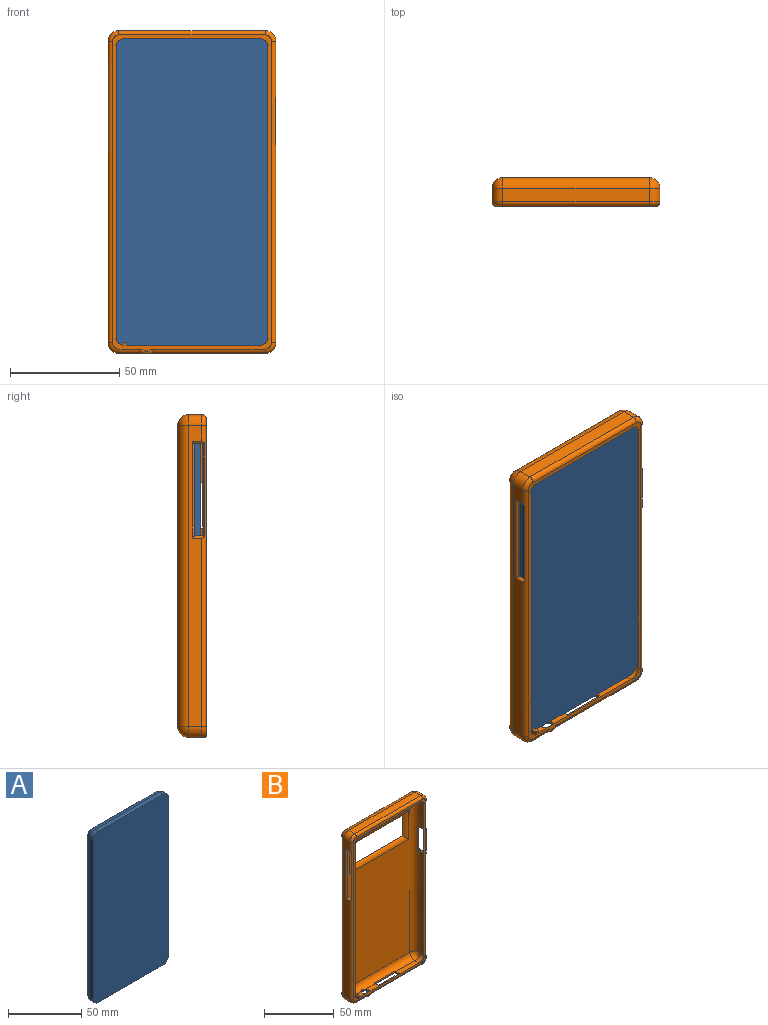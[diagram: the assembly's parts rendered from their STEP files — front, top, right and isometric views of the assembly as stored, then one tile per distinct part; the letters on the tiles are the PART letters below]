
ASSEMBLY  parts=2 mates=1
PART A: 18 faces, bbox 72.1x8.3x142.4 mm
  f0: plane 132.24x3.22mm, normal (1,0,0), area 425.8mm2, adj f4,f6,f9,f10
  f1: plane 61.94x3.22mm, normal (0,0,1), area 199.4mm2, adj f4,f6,f7,f13
  f2: plane 132.24x3.22mm, normal (-1,0,0), area 425.8mm2, adj f4,f7,f8,f17
  f3: plane 61.94x3.22mm, normal (0,0,-1), area 199.4mm2, adj f4,f8,f9,f14
  f4: plane 142.4x72.1mm, normal (0,-1,0), area 10244.9mm2, adj f0,f1,f2,f3,f6,f7,f8,f9
  f5: plane 132.24x61.94mm, normal (0,1,0), area 8190.9mm2, adj f10,f13,f14,f17
  f6: cylinder r=5.08mm len=5.08mm, axis (0,-1,0), area 25.7mm2, adj f0,f1,f4,f11
  f7: cylinder r=5.08mm len=5.08mm, axis (0,1,0), area 25.7mm2, adj f1,f2,f4,f15
  f8: cylinder r=5.08mm len=5.08mm, axis (0,-1,0), area 25.7mm2, adj f2,f3,f4,f16
  f9: cylinder r=5.08mm len=5.08mm, axis (0,1,0), area 25.7mm2, adj f0,f3,f4,f12
  f10: cylinder r=5.08mm len=132.24mm, axis (0,0,1), area 1055.2mm2, adj f0,f5,f11,f12
  f11: sphere r=5.08mm, area 40.5mm2, adj f6,f10,f13
  f12: sphere r=5.08mm, area 40.5mm2, adj f9,f10,f14
  f13: cylinder r=5.08mm len=61.94mm, axis (-1,0,0), area 494.3mm2, adj f1,f5,f11,f15
  f14: cylinder r=5.08mm len=61.94mm, axis (1,0,0), area 494.3mm2, adj f3,f5,f12,f16
  f15: sphere r=5.08mm, area 40.5mm2, adj f7,f13,f17
  f16: sphere r=5.08mm, area 40.5mm2, adj f8,f14,f17
  f17: cylinder r=5.08mm len=132.24mm, axis (0,0,-1), area 1055.2mm2, adj f2,f5,f15,f16
PART B: 97 faces, bbox 77.8x13.5x148.8 mm
  f0: plane 25x6mm, normal (1,0,0), area 150mm2, adj f21,f25,f50,f90
  f1: plane 7.7x4.33mm, normal (0,0,1), area 28.7mm2, adj f6,f20,f56,f73
  f2: plane 89x4.33mm, normal (-1,0,0), area 385mm2, adj f11,f43,f67,f76
  f3: plane 24x4.33mm, normal (-1,0,0), area 103.8mm2, adj f11,f44,f64,f76
  f4: plane 5.25x4.33mm, normal (1,0,0), area 22.7mm2, adj f18,f39,f62,f80
  f5: plane 63x4.33mm, normal (0,0,-1), area 272.6mm2, adj f19,f62,f64,f78
  f6: plane 5.8x3mm, normal (1,0,0), area 16.6mm2, adj f1,f14,f70,f71,f73
  f7: plane 5.8x3mm, normal (-1,0,0), area 16.6mm2, adj f14,f68,f70,f71,f82
  f8: plane 50.68x4.33mm, normal (0,0,1), area 144.7mm2, adj f20,f52,f53,f55,f56,f67,f73
  f9: plane 138x67mm, normal (0,1,0), area 8310mm2, adj f25,f28,f29,f32,f93,f94,f95,f96
  f10: plane 134x63mm, normal (0,-1,0), area 6857.4mm2, adj f11,f18,f19,f20,f93,f94,f95,f96
  f11: cylinder r=5mm len=134mm, axis (0,0,1), area 1004.6mm2, adj f2,f3,f10,f42,f43,f44,f65,f66
  f12: plane 138x6mm, normal (-1,0,0), area 628.3mm2, adj f22,f23,f32,f35,f36,f39,f87
  f13: plane 84.38x4.33mm, normal (1,0,0), area 365.1mm2, adj f18,f35,f68,f80
  f14: plane 144.95x73mm, normal (0,-1,0), area 768mm2, adj f6,f7,f71,f73,f75,f76,f77,f78
  f15: plane 90x6mm, normal (1,0,0), area 540mm2, adj f24,f25,f46,f90
  f16: plane 67x6mm, normal (0,0,1), area 402mm2, adj f21,f22,f29,f91
  f17: plane 67x6mm, normal (0,0,-1), area 245.2mm2, adj f23,f24,f28,f58,f59,f60,f61,f83
  f18: cylinder r=5mm len=134mm, axis (0,0,-1), area 1026.5mm2, adj f4,f10,f13,f38,f40,f41,f63,f69
  f19: cylinder r=5mm len=63mm, axis (-1,0,0), area 494.8mm2, adj f5,f10,f63,f65
  f20: cylinder r=5mm len=63mm, axis (1,0,0), area 471.5mm2, adj f1,f8,f10,f53,f54,f55,f56,f66
  f21: cylinder r=5mm len=6mm, axis (0,1,0), area 47.1mm2, adj f0,f16,f27,f92
  f22: cylinder r=5mm len=6mm, axis (0,-1,0), area 47.1mm2, adj f12,f16,f31,f89
  f23: cylinder r=5mm len=6mm, axis (0,1,0), area 47.1mm2, adj f12,f17,f30,f85
  f24: cylinder r=5mm len=6mm, axis (0,-1,0), area 47.1mm2, adj f15,f17,f26,f88
  f25: cylinder r=5mm len=138mm, axis (0,0,1), area 1054.8mm2, adj f0,f9,f15,f26,f27,f47,f49,f51
  f26: sphere r=5mm, area 39.3mm2, adj f24,f25,f28
  f27: sphere r=5mm, area 39.3mm2, adj f21,f25,f29
  f28: cylinder r=5mm len=67mm, axis (1,0,0), area 526.2mm2, adj f9,f17,f26,f30
  f29: cylinder r=5mm len=67mm, axis (-1,0,0), area 526.2mm2, adj f9,f16,f27,f31
  f30: sphere r=5mm, area 39.3mm2, adj f23,f28,f32
  f31: sphere r=5mm, area 39.3mm2, adj f22,f29,f32
  f32: cylinder r=5mm len=138mm, axis (0,0,-1), area 1083.8mm2, adj f9,f12,f30,f31
  f33: plane 44.37x1mm, normal (0,1,0), area 42.8mm2, adj f35,f37,f39,f81
  f34: plane 42.37x0.04mm, normal (0,-1,0), area 1.7mm2, adj f35,f36,f39,f41
  f35: cylinder r=1mm len=5.6mm, axis (0,1,0), area 14.3mm2, adj f12,f13,f33,f34,f36,f37,f38,f41
  f36: cylinder r=1mm len=44.37mm, axis (0,0,1), area 68.1mm2, adj f12,f34,f35,f39
  f37: cylinder r=1mm len=42.88mm, axis (0,0,-1), area 31.2mm2, adj f33,f35,f39,f87
  f38: torus R=6mm, axis (0,0,-1), area 0.2mm2, adj f18,f35,f41
  f39: cylinder r=1mm len=5.6mm, axis (0,-1,0), area 14.3mm2, adj f4,f12,f33,f34,f36,f37,f40,f41
  f40: torus R=6mm, axis (0,0,1), area 0.2mm2, adj f18,f39,f41
  f41: cylinder r=1mm len=44.37mm, axis (0,0,-1), area 62.8mm2, adj f18,f34,f35,f38,f39,f40
  f42: plane 21x1.38mm, normal (0,-1,0), area 29mm2, adj f11,f43,f44,f49
  f43: plane 6.58x1.51mm, normal (0,0,1), area 6.9mm2, adj f2,f11,f42,f45,f46,f47,f49,f72
  f44: plane 6.58x1.51mm, normal (0,0,-1), area 6.9mm2, adj f3,f11,f42,f45,f49,f50,f51,f72
  f45: plane 21x1mm, normal (0,1,0), area 21mm2, adj f43,f44,f48,f72
  f46: cylinder r=1mm len=6.93mm, axis (0,1,0), area 10.4mm2, adj f15,f43,f47,f48,f90
  f47: torus R=4mm, axis (0,0,1), area 0.8mm2, adj f25,f43,f46,f49
  f48: cylinder r=1mm len=21.72mm, axis (0,0,-1), area 18.7mm2, adj f45,f46,f50,f90
  f49: cylinder r=1mm len=23mm, axis (0,0,1), area 39.6mm2, adj f25,f42,f43,f44,f47,f51
  f50: cylinder r=1mm len=6.93mm, axis (0,-1,0), area 10.4mm2, adj f0,f44,f48,f51,f90
  f51: torus R=4mm, axis (0,0,1), area 0.8mm2, adj f25,f44,f49,f50
  f52: plane 21x1.3mm, normal (0,1,0), area 27.3mm2, adj f8,f53,f55,f57
  f53: plane 4.24x1.38mm, normal (1,0,0), area 5.5mm2, adj f8,f20,f52,f54,f58
  f54: plane 21x1.38mm, normal (0,-1,0), area 29.1mm2, adj f20,f53,f55,f60
  f55: plane 4.24x1.38mm, normal (-1,0,0), area 5.5mm2, adj f8,f20,f52,f54,f59
  f56: cylinder r=3mm len=6mm, axis (0,0,-1), area 24.5mm2, adj f1,f8,f20,f61,f74
  f57: cylinder r=0.7mm len=22.23mm, axis (1,0,0), area 21.9mm2, adj f52,f58,f59,f86
  f58: cylinder r=0.7mm len=5.56mm, axis (0,-1,0), area 5.2mm2, adj f17,f53,f57,f60,f86
  f59: cylinder r=0.7mm len=5.56mm, axis (0,1,0), area 5.2mm2, adj f17,f55,f57,f60,f86
  f60: cylinder r=0.7mm len=22.4mm, axis (-1,0,0), area 23.9mm2, adj f17,f54,f58,f59
  f61: torus R=3.7mm, axis (0,0,-1), area 22.5mm2, adj f17,f56,f84
  f62: cylinder r=5mm len=5mm, axis (0,-1,0), area 34mm2, adj f4,f5,f63,f79
  f63: sphere r=5mm, area 39.3mm2, adj f18,f19,f62
  f64: cylinder r=5mm len=5mm, axis (0,1,0), area 34mm2, adj f3,f5,f65,f77
  f65: sphere r=5mm, area 39.3mm2, adj f11,f19,f64
  f66: sphere r=5mm, area 39.3mm2, adj f11,f20,f67
  f67: cylinder r=5mm len=5mm, axis (0,-1,0), area 34mm2, adj f2,f8,f66,f75
  f68: cylinder r=5mm len=5mm, axis (0,1,0), area 34mm2, adj f7,f13,f69,f82
  f69: sphere r=5mm, area 39.3mm2, adj f18,f20,f68
  f70: plane 3x1.38mm, normal (0,1,0), area 4.1mm2, adj f6,f7,f20,f71
  f71: plane 5.8x1.38mm, normal (0,0,1), area 8mm2, adj f6,f7,f14,f70
  f72: plane 21x0.05mm, normal (1,0,0), area 0.9mm2, adj f43,f44,f45,f76
  f73: cylinder r=2.05mm len=61.62mm, axis (1,0,0), area 151.7mm2, adj f1,f6,f8,f14,f74,f75
  f74: plane 3.24x0.47mm, normal (0,0,-1), area 1mm2, adj f56,f73
  f75: torus R=3.03mm, axis (0,-1,0), area 16.5mm2, adj f14,f67,f73,f76
  f76: cylinder r=2.05mm len=134mm, axis (0,0,1), area 329.8mm2, adj f2,f3,f14,f72,f75,f77
  f77: torus R=3.03mm, axis (0,-1,0), area 16.5mm2, adj f14,f64,f76,f78
  f78: cylinder r=2.05mm len=63mm, axis (-1,0,0), area 155.1mm2, adj f5,f14,f77,f79
  f79: torus R=3.03mm, axis (0,-1,0), area 16.5mm2, adj f14,f62,f78,f80
  f80: cylinder r=2.05mm len=134mm, axis (0,0,-1), area 329.8mm2, adj f4,f13,f14,f79,f81,f82
  f81: plane 44.37x0.32mm, normal (-1,0,0), area 14.3mm2, adj f33,f35,f39,f80
  f82: torus R=3.03mm, axis (0,-1,0), area 16.5mm2, adj f7,f14,f68,f80
  f83: cylinder r=2mm len=9.59mm, axis (-1,0,0), area 30.1mm2, adj f14,f17,f84,f85
  f84: bspline ~7.27x2.26mm, area 11.8mm2, adj f14,f61,f83,f86
  f85: torus R=3mm, axis (0,-1,0), area 21.1mm2, adj f14,f23,f83,f87
  f86: cylinder r=2mm len=51.19mm, axis (-1,0,0), area 157.6mm2, adj f14,f17,f57,f58,f59,f84,f88
  f87: cylinder r=2mm len=138mm, axis (0,0,1), area 382.5mm2, adj f12,f14,f35,f37,f39,f85,f89
  f88: torus R=3mm, axis (0,-1,0), area 21.1mm2, adj f14,f24,f86,f90
  f89: torus R=3mm, axis (0,-1,0), area 21.1mm2, adj f14,f22,f87,f91
  f90: cylinder r=2mm len=138mm, axis (0,0,-1), area 411.8mm2, adj f0,f14,f15,f46,f48,f50,f88,f92
  f91: cylinder r=2mm len=67mm, axis (1,0,0), area 210.5mm2, adj f14,f16,f89,f92
  f92: torus R=3mm, axis (0,-1,0), area 21.1mm2, adj f14,f21,f90,f91
  f93: cylinder r=5mm len=60.29mm, axis (-1,0,0), area 272.3mm2, adj f9,f10,f94,f95
  f94: cylinder r=5mm len=26.29mm, axis (0,0,-1), area 106.3mm2, adj f9,f10,f93,f96
  f95: cylinder r=5mm len=26.29mm, axis (0,0,-1), area 106.3mm2, adj f9,f10,f93,f96
  f96: cylinder r=5mm len=60.29mm, axis (-1,0,0), area 272.3mm2, adj f9,f10,f94,f95
PLACE A t=(6.7,15.38,-89.92)mm
PLACE B t=(44.67,17.58,-164.8)mm
MATE planar A.f6 <-> B.f64  axis (0,1,0) through (37.67,15.38,-23.8)mm
